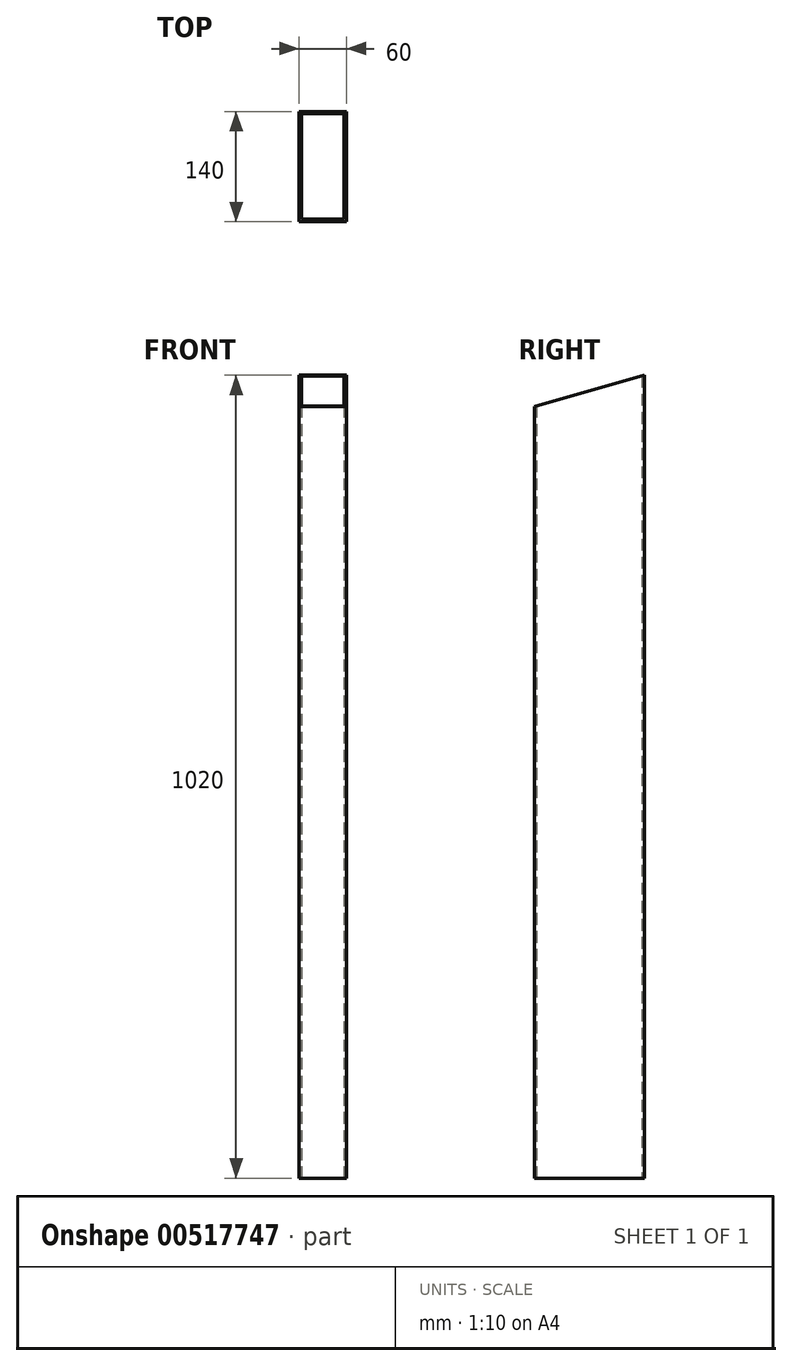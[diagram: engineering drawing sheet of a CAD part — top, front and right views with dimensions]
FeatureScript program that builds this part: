
annotation { "Feature Type Name" : "Feature", "Feature Type Description" : "" }
export const myFeature = defineFeature(function(context is Context, id is Id, definition is map)
    precondition{}
    {
        {
            var Q0;
            Q0=qCreatedBy(makeId("Right.planeOp"),FACE);
            var sketch = newSketch(context, id + "F0", { "sketchPlane" : qUnion([Q0])});
            skLineSegment(sketch, "E0", {"start": v(0, 0) * mm, "end": v(140, 0) * mm});
            skLineSegment(sketch, "E1", {"start": v(140, 0) * mm, "end": v(140, 1020) * mm});
            skLineSegment(sketch, "E2", {"start": v(140, 1020) * mm, "end": v(0, 980) * mm});
            skLineSegment(sketch, "E3", {"start": v(0, 980) * mm, "end": v(0, 0) * mm});
            skSolve(sketch);
        }
        {
            var Q0;
            Q0=qSketchRegion(id+"F0",true);
            extrude(context, id + "F1", {"entities" : qUnion([Q0]), "depth" : 60 * mm, "offsetDistance" : 25 * mm});
        }
        {
            var Q0;
            Q0=makeQuery(id+"F1.opExtrude","SWEPT_FACE",FACE,{"disambiguationData":[OSD([sQuery(id+"F0.wireOp",EDGE,"E0")])]});
            var sketch = newSketch(context, id + "F2", { "sketchPlane" : qUnion([Q0])});
            skLineSegment(sketch, "E4.bottom", {"start": v(0, 0) * mm, "end": v(3, 0) * mm});
            skLineSegment(sketch, "E4.top", {"start": v(0, -3) * mm, "end": v(3, -3) * mm});
            skLineSegment(sketch, "E4.left", {"start": v(0, 0) * mm, "end": v(0, -3) * mm});
            skLineSegment(sketch, "E4.right", {"start": v(3, 0) * mm, "end": v(3, -3) * mm});
            skLineSegment(sketch, "E5.bottom", {"start": v(3, -3) * mm, "end": v(57, -3) * mm});
            skLineSegment(sketch, "E5.top", {"start": v(3, -137) * mm, "end": v(57, -137) * mm});
            skLineSegment(sketch, "E5.left", {"start": v(3, -3) * mm, "end": v(3, -137) * mm});
            skLineSegment(sketch, "E5.right", {"start": v(57, -3) * mm, "end": v(57, -137) * mm});
            skSolve(sketch);
        }
        {
            var Q0;
            Q0=makeQuery(id+"F2.imprint","IMPRINT",FACE,{"disambiguationData":[TD([[makeQuery(id+"F2.imprint","IMPRINT",EDGE,{"derivedFrom":sQuery(id+"F2.wireOp",EDGE,"E5.bottom")}),-1.0]])]});
            extrude(context, id + "F3", {"entities" : qUnion([Q0]), "operationType" : NewBodyOperationType.REMOVE, "endBound" : BoundingType.THROUGH_ALL, "oppositeDirection" : true, "depth" : 25 * mm, "offsetDistance" : 25 * mm});
        }
    });
